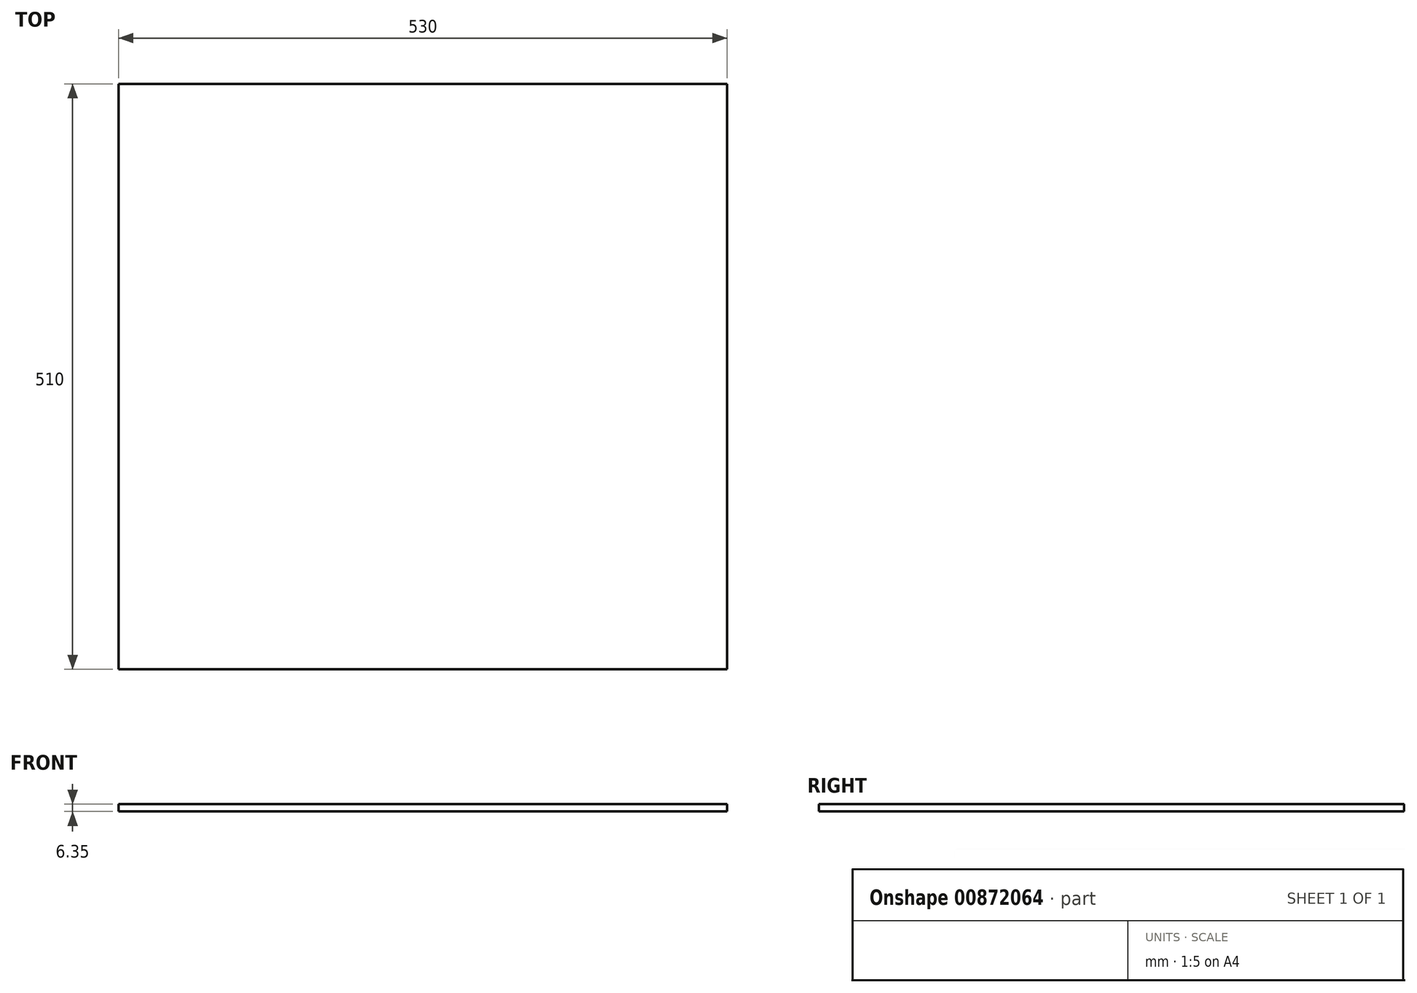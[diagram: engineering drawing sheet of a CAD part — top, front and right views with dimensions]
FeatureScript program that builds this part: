
annotation { "Feature Type Name" : "Feature", "Feature Type Description" : "" }
export const myFeature = defineFeature(function(context is Context, id is Id, definition is map)
    precondition{}
    {
        {
            var Q0;
            Q0=qCreatedBy(makeId("Top.planeOp"),FACE);
            var sketch = newSketch(context, id + "F0", { "sketchPlane" : qUnion([Q0])});
            skLineSegment(sketch, "E0.bottom", {"start": v(0, 0) * mm, "end": v(530, 0) * mm});
            skLineSegment(sketch, "E0.top", {"start": v(0, 510) * mm, "end": v(530, 510) * mm});
            skLineSegment(sketch, "E0.left", {"start": v(0, 0) * mm, "end": v(0, 510) * mm});
            skLineSegment(sketch, "E0.right", {"start": v(530, 0) * mm, "end": v(530, 510) * mm});
            skSolve(sketch);
        }
        {
            var Q0;
            Q0=makeQuery(id+"F0.imprint","IMPRINT",FACE,{"disambiguationData":[TD([[makeQuery(id+"F0.imprint","IMPRINT",EDGE,{"derivedFrom":sQuery(id+"F0.wireOp",EDGE,"E0.bottom")}),1.0]])]});
            extrude(context, id + "F1", {"entities" : qUnion([Q0]), "depth" : -6.35 * mm, "offsetDistance" : 25 * mm});
        }
    });
